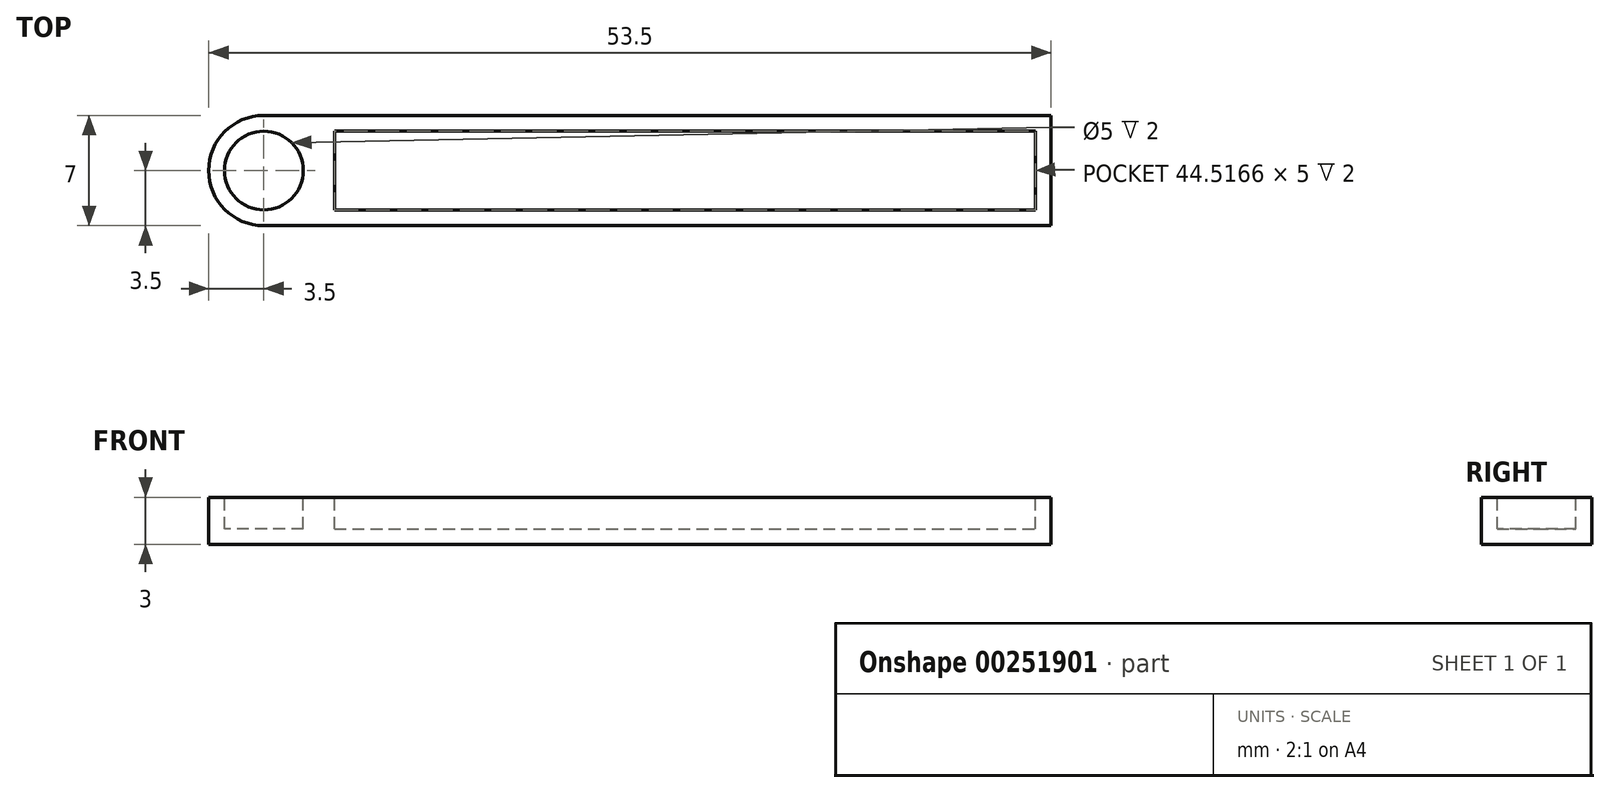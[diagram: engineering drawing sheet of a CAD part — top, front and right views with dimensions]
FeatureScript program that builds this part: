
annotation { "Feature Type Name" : "Feature", "Feature Type Description" : "" }
export const myFeature = defineFeature(function(context is Context, id is Id, definition is map)
    precondition{}
    {
        {
            var Q0;
            Q0=qCreatedBy(makeId("Top.planeOp"),FACE);
            var sketch = newSketch(context, id + "F0", { "sketchPlane" : qUnion([Q0])});
            skArc(sketch, "E0", {"start": v(0, 3.5) * mm, "mid": v(-3.5, 0) * mm, "end": v(0, -3.5) * mm});
            skLineSegment(sketch, "E1", {"start": v(0, 3.5) * mm, "end": v(0, -3.5) * mm, "construction": true});
            skLineSegment(sketch, "E2", {"start": v(0, -3.5) * mm, "end": v(50, -3.5) * mm});
            skLineSegment(sketch, "E3", {"start": v(0, 3.5) * mm, "end": v(50, 3.5) * mm});
            skLineSegment(sketch, "E4", {"start": v(50, 3.5) * mm, "end": v(50, -3.5) * mm});
            skSolve(sketch);
        }
        {
            var Q0;
            Q0 = qSketchRegion(id + "F0", true);
            extrude(context, id + "F1", {"entities" : qUnion([Q0]), "depth" : 3 * mm});
        }
        {
            var Q0;
            Q0=makeQuery(id+"F1.opExtrude","CAP_FACE",FACE,{"disambiguationData":[OSD([sQuery(id+"F0.wireOp",EDGE,"E0"),sQuery(id+"F0.wireOp",EDGE,"E2"),sQuery(id+"F0.wireOp",EDGE,"E3"),sQuery(id+"F0.wireOp",EDGE,"E4")])],"isStart":false});
            var sketch = newSketch(context, id + "F2", { "sketchPlane" : qUnion([Q0])});
            skCircle(sketch, "E5", {"center": v(0, 0) * mm, "radius": 2.5 * mm});
            skLineSegment(sketch, "E6.bottom", {"start": v(4.48, 2.5) * mm, "end": v(49, 2.5) * mm});
            skLineSegment(sketch, "E6.top", {"start": v(4.48, -2.5) * mm, "end": v(49, -2.5) * mm});
            skLineSegment(sketch, "E6.left", {"start": v(4.48, 2.5) * mm, "end": v(4.48, -2.5) * mm});
            skLineSegment(sketch, "E6.right", {"start": v(49, 2.5) * mm, "end": v(49, -2.5) * mm});
            skSolve(sketch);
        }
        {
            var Q0;
            Q0 = qSketchRegion(id + "F2", true);
            extrude(context, id + "F3", {"entities" : qUnion([Q0]), "operationType" : NewBodyOperationType.REMOVE, "oppositeDirection" : true, "depth" : 2 * mm});
        }
    });
